# Revit family: SQUARE II RAIL SHOWER WITH OVERHEAD
name_source: partatom
category: Plumbing Fixtures
units: mm (PartAtom-declared; Revit-internal decimal feet)

## family parameters
Cut with Voids When Loaded = No
Host = Face
OmniClass Number = 23.45.05.14.17
OmniClass Title = Showers
Part Type = Normal
Room Calculation Point = No
Round Connector Dimension = Use Diameter
Shared = No

## types (2) — shared parameters
Assembly Code = D2010710
Manufacturer = GWA Bathrooms & Kitchens
Shower Nozzels = GWA-Plastic-General
URL = https://www.clark.com.au
Vent Connection = No
Waste Connection = No
zero-valued in all types: Default Elevation

## per-type parameters (varying)
| type | Flexible Rod | Model | Shower Head | Shower Rod |
| CLARK SQUARE II RAIL SHOWER WITH OVERHEAD - CHROME | GWA_Metal-Chrome | CL10074-C3A | GWA_Metal-Chrome | GWA_Metal-Chrome |
| CLARK SQUARE II RAIL SHOWER WITH OVERHEAD - MATTE BLACK | GWA-Metal-Black | CL10074-B3A | GWA-Metal-Black | GWA-Metal-Black |

note: column(s) folded — value = type name in every type: Description

## geometry (parser evidence)
native form markers: Sweep x2
no freeform markers — native parametric forms only
